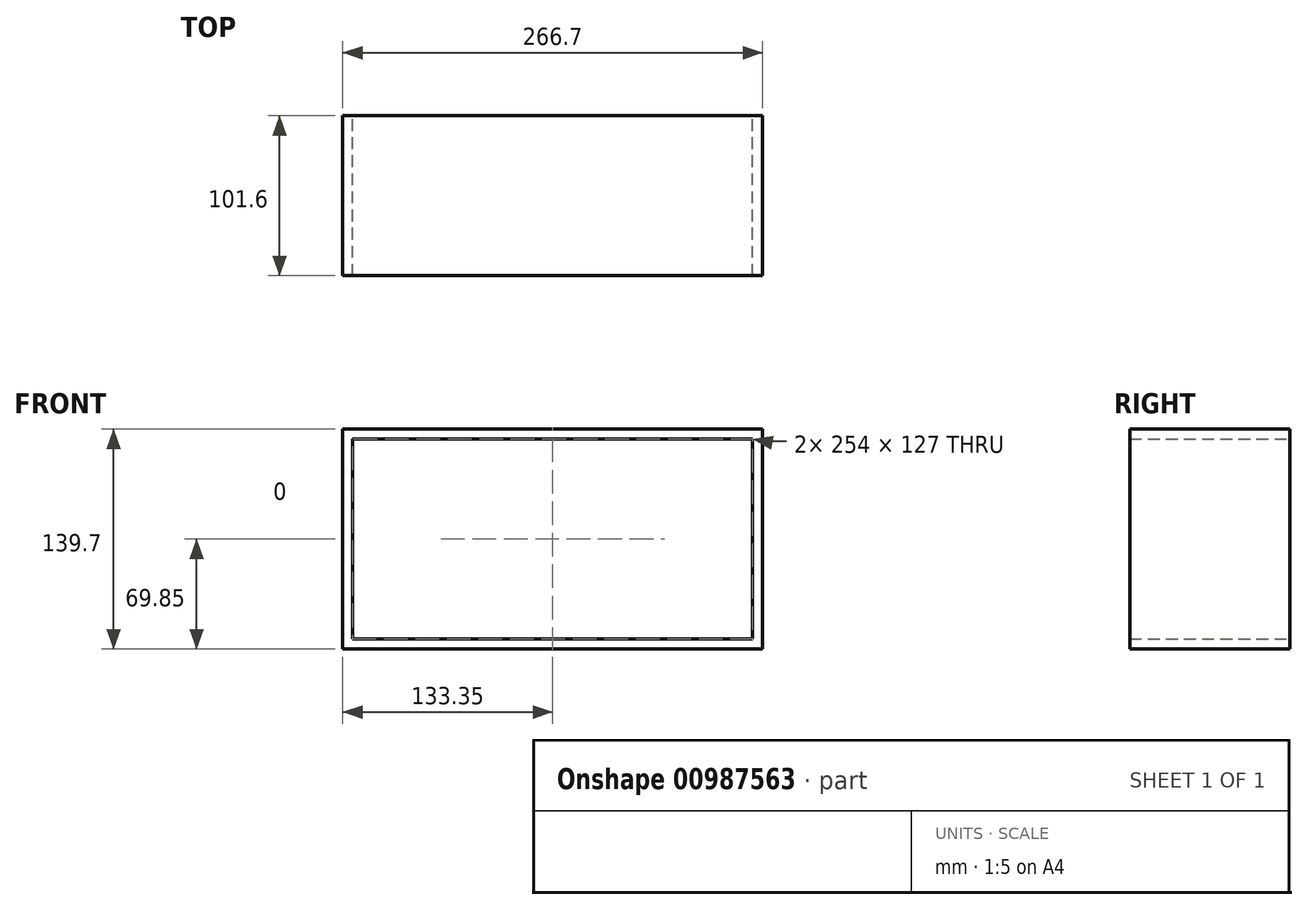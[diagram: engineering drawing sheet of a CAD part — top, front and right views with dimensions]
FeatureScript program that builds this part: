
annotation { "Feature Type Name" : "Feature", "Feature Type Description" : "" }
export const myFeature = defineFeature(function(context is Context, id is Id, definition is map)
    precondition{}
    {
        {
            var Q0;
            Q0=qCreatedBy(makeId("Front.planeOp"),FACE);
            var sketch = newSketch(context, id + "F0", { "sketchPlane" : qUnion([Q0])});
            skLineSegment(sketch, "E0.bottom", {"start": v(-127, -63.5) * mm, "end": v(127, -63.5) * mm});
            skLineSegment(sketch, "E0.top", {"start": v(-127, 63.5) * mm, "end": v(127, 63.5) * mm});
            skLineSegment(sketch, "E0.left", {"start": v(-127, -63.5) * mm, "end": v(-127, 63.5) * mm});
            skLineSegment(sketch, "E0.right", {"start": v(127, -63.5) * mm, "end": v(127, 63.5) * mm});
            skSolve(sketch);
        }
        {
            var Q0;
            Q0=qCreatedBy(makeId("Front.planeOp"),FACE);
            var sketch = newSketch(context, id + "F1", { "sketchPlane" : qUnion([Q0])});
            skLineSegment(sketch, "E1.bottom", {"start": v(-133.35, 69.85) * mm, "end": v(133.35, 69.85) * mm});
            skLineSegment(sketch, "E1.top", {"start": v(-133.35, -69.85) * mm, "end": v(133.35, -69.85) * mm});
            skLineSegment(sketch, "E1.left", {"start": v(-133.35, 69.85) * mm, "end": v(-133.35, -69.85) * mm});
            skLineSegment(sketch, "E1.right", {"start": v(133.35, 69.85) * mm, "end": v(133.35, -69.85) * mm});
            skSolve(sketch);
        }
        {
            var Q0;
            Q0 = qSketchRegion(id + "F1", true);
            extrude(context, id + "F2", {"entities" : qUnion([Q0]), "depth" : 101.6 * mm, "offsetDistance" : 25.4 * mm});
        }
        {
            var Q0;
            Q0 = qSketchRegion(id + "F0", true);
            extrude(context, id + "F3", {"entities" : qUnion([Q0]), "operationType" : NewBodyOperationType.REMOVE, "endBound" : BoundingType.THROUGH_ALL, "depth" : 25.4 * mm, "offsetDistance" : 25.4 * mm});
        }
        {
            var Q0;
            Q0=makeQuery(id+"F2.opExtrude","SWEPT_BODY",BODY,{"disambiguationData":[OSD([sQuery(id+"F1.wireOp",EDGE,"E1.bottom"),sQuery(id+"F1.wireOp",EDGE,"E1.top"),sQuery(id+"F1.wireOp",EDGE,"E1.left"),sQuery(id+"F1.wireOp",EDGE,"E1.right")])]});
            transform(context, id + "F4", {"entities" : qUnion([Q0]), "transformType" : TransformType.TRANSLATION_3D, "dx" : 0 * mm, "dy" : 0 * mm, "dz" : 0 * mm, "makeCopy" : true});
        }
    });
